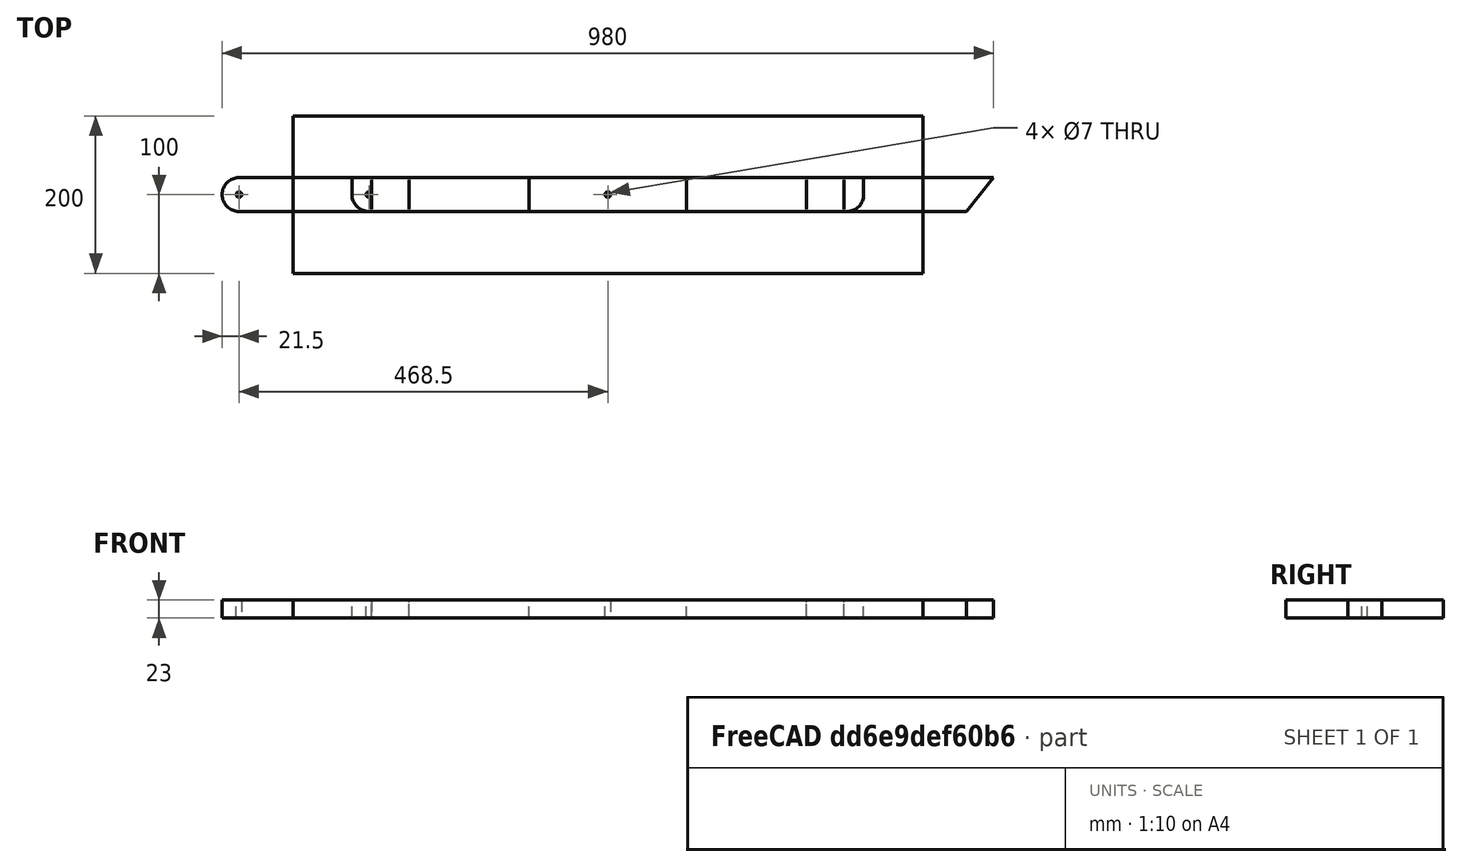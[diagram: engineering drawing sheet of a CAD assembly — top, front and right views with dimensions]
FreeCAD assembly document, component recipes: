
FREECAD ASSEMBLY — COMPONENT RECIPES ("montagem_mesa")

This assembly document has 14 components, labeled P0..P13 below (a component is one placed body or linked part). 14 of them carry a construction recipe — the FreeCAD feature program that regenerates the part from scratch, quoted from this document or its linked companion documents; the rest are supplied as boundary geometry only. No exploded tour is included for this assembly.
COMPONENT P0 — recipe-attached ("pe1.1", modeled in this document).
Construction recipe (the document's own serialized feature program — sketch geometry with constraints, then the solid features built on it; lengths are millimeters unless a unit is written):

FEATURE [Sketcher::SketchObject] Sketch
  FullyConstrained = true
  MapMode = 5
  Support = -> [XY_Plane]
  sketch-geometry (5):
    g0: LineSegment StartX=490 StartY=-21.5 StartZ=0 EndX=490 EndY=21.5 EndZ=0
    g1: LineSegment StartX=490 StartY=21.5 StartZ=0 EndX=-490 EndY=21.5 EndZ=0
    g2: LineSegment StartX=-490 StartY=21.5 StartZ=0 EndX=-490 EndY=-21.5 EndZ=0
    g3: LineSegment StartX=-490 StartY=-21.5 StartZ=0 EndX=490 EndY=-21.5 EndZ=0
    g4: GeomPoint X=0 Y=0 Z=0
  constraints (12):
    c: Coincident(g0,g1)
    c: Coincident(g1,g2)
    c: Coincident(g2,g3)
    c: Coincident(g3,g0)
    c: Horizontal(g1)
    c: Horizontal(g3)
    c: Vertical(g0)
    c: Vertical(g2)
    c: Symmetric(g1,g0,g4)
    c: Coincident(g4,g-1)
    c: DistanceY(g2,g2) = 43
    c: DistanceX(g1,g1) = 980
FEATURE [PartDesign::Pad] Pad
  Direction = (0,0,1)
  Length = 23
  Length2 = 10
  Profile = -> Sketch
  ReferenceAxis = -> Sketch [N_Axis]
  Type = 0
FEATURE [Sketcher::SketchObject] Sketch003
  FullyConstrained = true
  MapMode = 5
  Placement = pos=(0,0,23) rot=(0,0,1;0rad)
  Support = -> [Pad]
  sketch-geometry (1):
    g0: Circle CenterX=0 CenterY=0 CenterZ=0 NormalX=0 NormalY=0 NormalZ=1 AngleXU=0 Radius=3.5
  constraints (2):
    c: Coincident(g0,g-1)
    c: Diameter(g0) = 7
FEATURE [PartDesign::Pocket] Pocket001
  BaseFeature = -> Pad
  Direction = (0,0,-1)
  Length = 5
  Length2 = 5
  Profile = -> Sketch003
  ReferenceAxis = -> Sketch003 [N_Axis]
  Type = 1
FEATURE [PartDesign::Fillet] Fillet001
  Base = -> Pocket001 [Edge5,Edge8]
  BaseFeature = -> Pocket001
  Radius = 21.49
  SupportTransform = false
  UseAllEdges = false
FEATURE [Sketcher::SketchObject] Sketch015
  FullyConstrained = false
  MapMode = 5
  Placement = pos=(0,0,23) rot=(0,0,1;0rad)
  sketch-geometry (3):
    g0: LineSegment StartX=490 StartY=21.5 StartZ=0 EndX=455.575 EndY=-21.5 EndZ=0
    g1: LineSegment StartX=455.575 StartY=-21.5 StartZ=0 EndX=490 EndY=-21.5 EndZ=0
    g2: LineSegment StartX=490 StartY=-21.5 StartZ=0 EndX=490 EndY=21.5 EndZ=0
  constraints (4):
    c: Coincident(g0,g1)
    c: Coincident(g1,g2)
    c: Coincident(g2,g0)
    c: Angle(g0,g2) = 0.675093
FEATURE [PartDesign::Pocket] Pocket007
  BaseFeature = -> Fillet001
  Direction = (0,0,-1)
  Length = 5
  Length2 = 5
  Profile = -> Sketch015
  ReferenceAxis = -> Sketch015 [N_Axis]
  Type = 1
FEATURE [PartDesign::Body] Body  label="p1"
  Group = -> [Sketch,Pad,Sketch003,Pocket001,Fillet001,Sketch015,Pocket007]
  Origin = -> Origin
  Tip = -> Pocket007
COMPONENT P1 — same part as P0; its construction recipe is shown at P0.
COMPONENT P2 — recipe-attached ("trave1.1", modeled in this document).
Construction recipe (the document's own serialized feature program — sketch geometry with constraints, then the solid features built on it; lengths are millimeters unless a unit is written):

FEATURE [Sketcher::SketchObject] Sketch006
  FullyConstrained = true
  MapMode = 5
  Support = -> [XY_Plane003]
  sketch-geometry (5):
    g0: LineSegment StartX=-252.5 StartY=21.5 StartZ=0 EndX=-252.5 EndY=-21.5 EndZ=0
    g1: LineSegment StartX=-252.5 StartY=-21.5 StartZ=0 EndX=252.5 EndY=-21.5 EndZ=0
    g2: LineSegment StartX=252.5 StartY=-21.5 StartZ=0 EndX=252.5 EndY=21.5 EndZ=0
    g3: LineSegment StartX=252.5 StartY=21.5 StartZ=0 EndX=-252.5 EndY=21.5 EndZ=0
    g4: GeomPoint X=0 Y=0 Z=0
  constraints (12):
    c: Coincident(g0,g1)
    c: Coincident(g1,g2)
    c: Coincident(g2,g3)
    c: Coincident(g3,g0)
    c: Horizontal(g1)
    c: Horizontal(g3)
    c: Vertical(g0)
    c: Vertical(g2)
    c: Symmetric(g1,g0,g4)
    c: Coincident(g4,g-1)
    c: DistanceX(g3,g3) = 505
    c: DistanceY(g0,g0) = 43
FEATURE [PartDesign::Pad] Pad003
  Direction = (0,0,1)
  Length = 23
  Length2 = 10
  Profile = -> Sketch006
  ReferenceAxis = -> Sketch006 [N_Axis]
  Type = 0
FEATURE [PartDesign::Fillet] Fillet003
  Base = -> Pad003 [Edge7,Edge6,Edge12,Edge11]
  BaseFeature = -> Pad003
  Radius = 3
  SupportTransform = false
  UseAllEdges = false
FEATURE [PartDesign::Body] Body003  label="p4"
  Group = -> [Sketch006,Pad003,Fillet003]
  Origin = -> Origin003
  Tip = -> Fillet003
COMPONENT P3 — same part as P2; its construction recipe is shown at P2.
COMPONENT P4 — recipe-attached ("pe2.1", modeled in this document).
Construction recipe (the document's own serialized feature program — sketch geometry with constraints, then the solid features built on it; lengths are millimeters unless a unit is written):

FEATURE [Sketcher::SketchObject] Sketch001
  FullyConstrained = true
  MapMode = 5
  Support = -> [XY_Plane001]
  sketch-geometry (5):
    g0: LineSegment StartX=-490 StartY=21.5 StartZ=0 EndX=-490 EndY=-21.5 EndZ=0
    g1: LineSegment StartX=-490 StartY=-21.5 StartZ=0 EndX=490 EndY=-21.5 EndZ=0
    g2: LineSegment StartX=490 StartY=-21.5 StartZ=0 EndX=490 EndY=21.5 EndZ=0
    g3: LineSegment StartX=490 StartY=21.5 StartZ=0 EndX=-490 EndY=21.5 EndZ=0
    g4: GeomPoint X=0 Y=0 Z=0
  constraints (12):
    c: Coincident(g0,g1)
    c: Coincident(g1,g2)
    c: Coincident(g2,g3)
    c: Coincident(g3,g0)
    c: Horizontal(g1)
    c: Horizontal(g3)
    c: Vertical(g0)
    c: Vertical(g2)
    c: Symmetric(g1,g0,g4)
    c: Coincident(g4,g-1)
    c: DistanceY(g0,g0) = 43
    c: DistanceX(g3,g3) = 980
FEATURE [PartDesign::Pad] Pad001
  Direction = (0,0,1)
  Length = 23
  Length2 = 10
  Profile = -> Sketch001
  ReferenceAxis = -> Sketch001 [N_Axis]
  Type = 0
FEATURE [Sketcher::SketchObject] Sketch002
  ExternalGeometry = -> [Pad001]
  FullyConstrained = true
  MapMode = 5
  Placement = pos=(0,0,23) rot=(0,0,1;0rad)
  Support = -> [Pad001]
  sketch-geometry (2):
    g0: Circle CenterX=0 CenterY=0 CenterZ=0 NormalX=0 NormalY=0 NormalZ=1 AngleXU=0 Radius=3.5
    g1: Circle CenterX=-468.5 CenterY=0 CenterZ=0 NormalX=0 NormalY=0 NormalZ=1 AngleXU=0 Radius=3.5
  constraints (5):
    c: Coincident(g0,g-1)
    c: Diameter(g0) = 7
    c: PointOnObject(g1,g-1)
    c: Diameter(g1) = 7
    c: DistanceX(g-3,g1) = 21.5
FEATURE [PartDesign::Pocket] Pocket
  BaseFeature = -> Pad001
  Direction = (0,0,-1)
  Length = 5
  Length2 = 5
  Profile = -> Sketch002
  ReferenceAxis = -> Sketch002 [N_Axis]
  Type = 1
FEATURE [PartDesign::Fillet] Fillet
  Base = -> Pocket [Edge1,Edge2]
  BaseFeature = -> Pocket
  Radius = 21.49
  SupportTransform = false
  UseAllEdges = false
FEATURE [Sketcher::SketchObject] Sketch014
  ExternalGeometry = -> [Fillet]
  FullyConstrained = true
  MapMode = 5
  Placement = pos=(0,0,23) rot=(0,0,1;0rad)
  Support = -> [Fillet]
  sketch-geometry (3):
    g0: LineSegment StartX=490 StartY=21.5 StartZ=0 EndX=455.575 EndY=-21.5 EndZ=0
    g1: LineSegment StartX=455.575 StartY=-21.5 StartZ=0 EndX=490 EndY=-21.5 EndZ=0
    g2: LineSegment StartX=490 StartY=-21.5 StartZ=0 EndX=490 EndY=21.5 EndZ=0
  constraints (7):
    c: Coincident(g-3,g0)
    c: PointOnObject(g0,g-4)
    c: Coincident(g0,g1)
    c: Coincident(g1,g-4)
    c: Coincident(g1,g2)
    c: Coincident(g2,g0)
    c: Angle(g0,g2) = 0.675093
FEATURE [PartDesign::Pocket] Pocket006
  BaseFeature = -> Fillet
  Direction = (0,0,-1)
  Length = 5
  Length2 = 5
  Profile = -> Sketch014
  ReferenceAxis = -> Sketch014 [N_Axis]
  Type = 1
FEATURE [PartDesign::Body] Body001  label="p2"
  Group = -> [Sketch001,Pad001,Sketch002,Pocket,Fillet,Sketch014,Pocket006]
  Origin = -> Origin001
  Tip = -> Pocket006
COMPONENT P5 — same part as P4; its construction recipe is shown at P4.
COMPONENT P6 — recipe-attached ("base1", modeled in this document).
Construction recipe (the document's own serialized feature program — sketch geometry with constraints, then the solid features built on it; lengths are millimeters unless a unit is written):

FEATURE [Sketcher::SketchObject] Sketch004
  FullyConstrained = true
  MapMode = 5
  Support = -> [XY_Plane002]
  sketch-geometry (5):
    g0: LineSegment StartX=-325 StartY=-21.5 StartZ=0 EndX=-325 EndY=21.5 EndZ=0
    g1: LineSegment StartX=-325 StartY=21.5 StartZ=0 EndX=325 EndY=21.5 EndZ=0
    g2: LineSegment StartX=325 StartY=21.5 StartZ=0 EndX=325 EndY=-21.5 EndZ=0
    g3: LineSegment StartX=325 StartY=-21.5 StartZ=0 EndX=-325 EndY=-21.5 EndZ=0
    g4: GeomPoint X=0 Y=0 Z=0
  constraints (12):
    c: Coincident(g0,g1)
    c: Coincident(g1,g2)
    c: Coincident(g2,g3)
    c: Coincident(g3,g0)
    c: Horizontal(g1)
    c: Horizontal(g3)
    c: Vertical(g0)
    c: Vertical(g2)
    c: Symmetric(g1,g0,g4)
    c: Coincident(g4,g-1)
    c: DistanceX(g1,g1) = 650
    c: DistanceY(g0,g0) = 43
FEATURE [PartDesign::Pad] Pad002
  Direction = (0,0,1)
  Length = 23
  Length2 = 10
  Profile = -> Sketch004
  ReferenceAxis = -> Sketch004 [N_Axis]
  Type = 0
FEATURE [Sketcher::SketchObject] Sketch005
  ExternalGeometry = -> [Pad002]
  FullyConstrained = true
  MapMode = 5
  Placement = pos=(0,0,23) rot=(0,0,1;0rad)
  Support = -> [Pad002]
  sketch-geometry (1):
    g0: Circle CenterX=-303.5 CenterY=0 CenterZ=0 NormalX=0 NormalY=0 NormalZ=1 AngleXU=0 Radius=3.5
  constraints (3):
    c: PointOnObject(g0,g-1)
    c: DistanceX(g-3,g0) = 21.5
    c: Diameter(g0) = 7
FEATURE [PartDesign::Pocket] Pocket002
  BaseFeature = -> Pad002
  Direction = (0,0,-1)
  Length = 5
  Length2 = 5
  Profile = -> Sketch005
  ReferenceAxis = -> Sketch005 [N_Axis]
  Type = 1
FEATURE [PartDesign::Fillet] Fillet002
  Base = -> Pocket002 [Edge5,Edge1]
  BaseFeature = -> Pocket002
  Radius = 21.5
  SupportTransform = false
  UseAllEdges = false
FEATURE [PartDesign::Body] Body002  label="p3"
  Group = -> [Sketch004,Pad002,Sketch005,Pocket002,Fillet002]
  Origin = -> Origin002
  Tip = -> Fillet002
COMPONENT P7 — same part as P6; its construction recipe is shown at P6.
COMPONENT P8 — recipe-attached ("tábua1", modeled in this document).
Construction recipe (the document's own serialized feature program — sketch geometry with constraints, then the solid features built on it; lengths are millimeters unless a unit is written):

FEATURE [Sketcher::SketchObject] Sketch010
  FullyConstrained = true
  MapMode = 5
  Support = -> [XY_Plane004]
  sketch-geometry (5):
    g0: LineSegment StartX=-400 StartY=100 StartZ=0 EndX=-400 EndY=-100 EndZ=0
    g1: LineSegment StartX=-400 StartY=-100 StartZ=0 EndX=400 EndY=-100 EndZ=0
    g2: LineSegment StartX=400 StartY=-100 StartZ=0 EndX=400 EndY=100 EndZ=0
    g3: LineSegment StartX=400 StartY=100 StartZ=0 EndX=-400 EndY=100 EndZ=0
    g4: GeomPoint X=0 Y=0 Z=0
  constraints (12):
    c: Coincident(g0,g1)
    c: Coincident(g1,g2)
    c: Coincident(g2,g3)
    c: Coincident(g3,g0)
    c: Horizontal(g1)
    c: Horizontal(g3)
    c: Vertical(g0)
    c: Vertical(g2)
    c: Symmetric(g1,g0,g4)
    c: Coincident(g4,g-1)
    c: DistanceX(g3,g3) = 800
    c: DistanceY(g0,g0) = 200
FEATURE [PartDesign::Pad] Pad004
  Direction = (0,0,1)
  Length = 23
  Length2 = 10
  Profile = -> Sketch010
  ReferenceAxis = -> Sketch010 [N_Axis]
  Type = 0
FEATURE [PartDesign::Body] Body004  label="p5"
  Group = -> [Sketch010,Pad004]
  Origin = -> Origin004
  Tip = -> Pad004
COMPONENT P9 — same part as P8; its construction recipe is shown at P8.
COMPONENT P10 — same part as P8; its construction recipe is shown at P8.
COMPONENT P11 — same part as P8; its construction recipe is shown at P8.
COMPONENT P12 — recipe-attached ("trave2", modeled in this document).
Construction recipe (the document's own serialized feature program — sketch geometry with constraints, then the solid features built on it; lengths are millimeters unless a unit is written):

FEATURE [Sketcher::SketchObject] Sketch012
  FullyConstrained = true
  MapMode = 5
  Support = -> [XY_Plane005]
  sketch-geometry (5):
    g0: LineSegment StartX=-300 StartY=21.5 StartZ=0 EndX=-300 EndY=-21.5 EndZ=0
    g1: LineSegment StartX=-300 StartY=-21.5 StartZ=0 EndX=300 EndY=-21.5 EndZ=0
    g2: LineSegment StartX=300 StartY=-21.5 StartZ=0 EndX=300 EndY=21.5 EndZ=0
    g3: LineSegment StartX=300 StartY=21.5 StartZ=0 EndX=-300 EndY=21.5 EndZ=0
    g4: GeomPoint X=0 Y=0 Z=0
  constraints (12):
    c: Coincident(g0,g1)
    c: Coincident(g1,g2)
    c: Coincident(g2,g3)
    c: Coincident(g3,g0)
    c: Horizontal(g1)
    c: Horizontal(g3)
    c: Vertical(g0)
    c: Vertical(g2)
    c: Symmetric(g1,g0,g4)
    c: Coincident(g4,g-1)
    c: DistanceX(g3,g3) = 600
    c: DistanceY(g2,g2) = 43
FEATURE [PartDesign::Pad] Pad005
  Direction = (0,0,1)
  Length = 23
  Length2 = 10
  Profile = -> Sketch012
  ReferenceAxis = -> Sketch012 [N_Axis]
  Type = 0
FEATURE [PartDesign::Fillet] Fillet004
  Base = -> Pad005 [Edge12,Edge11,Edge7,Edge6]
  BaseFeature = -> Pad005
  Radius = 3
  SupportTransform = false
  UseAllEdges = false
FEATURE [PartDesign::Body] Body005  label="p6"
  Group = -> [Sketch012,Pad005,Fillet004]
  Origin = -> Origin005
  Tip = -> Fillet004
COMPONENT P13 — recipe-attached ("suporte", modeled in this document).
Construction recipe (the document's own serialized feature program — sketch geometry with constraints, then the solid features built on it; lengths are millimeters unless a unit is written):

FEATURE [Sketcher::SketchObject] Sketch013
  FullyConstrained = true
  MapMode = 5
  Support = -> [XY_Plane006]
  sketch-geometry (5):
    g0: LineSegment StartX=-100 StartY=21.5 StartZ=0 EndX=-100 EndY=-21.5 EndZ=0
    g1: LineSegment StartX=-100 StartY=-21.5 StartZ=0 EndX=100 EndY=-21.5 EndZ=0
    g2: LineSegment StartX=100 StartY=-21.5 StartZ=0 EndX=100 EndY=21.5 EndZ=0
    g3: LineSegment StartX=100 StartY=21.5 StartZ=0 EndX=-100 EndY=21.5 EndZ=0
    g4: GeomPoint X=0 Y=0 Z=0
  constraints (12):
    c: Coincident(g0,g1)
    c: Coincident(g1,g2)
    c: Coincident(g2,g3)
    c: Coincident(g3,g0)
    c: Horizontal(g1)
    c: Horizontal(g3)
    c: Vertical(g0)
    c: Vertical(g2)
    c: Symmetric(g1,g0,g4)
    c: Coincident(g4,g-1)
    c: DistanceX(g3,g3) = 200
    c: DistanceY(g2,g2) = 43
FEATURE [PartDesign::Pad] Pad006
  Direction = (0,0,1)
  Length = 23
  Length2 = 10
  Profile = -> Sketch013
  ReferenceAxis = -> Sketch013 [N_Axis]
  Type = 0
FEATURE [PartDesign::Body] Body006  label="p7"
  Group = -> [Sketch013,Pad006]
  Origin = -> Origin006
  Tip = -> Pad006
PROVENANCE & LICENSES
A FreeCAD (.FCStd) document from a public repository crawl; recipes are the document's own serialized feature recipes (and, for linked parts, companion documents' recipes).
License: as declared in the source repository (recorded in the dataset sidecar).
